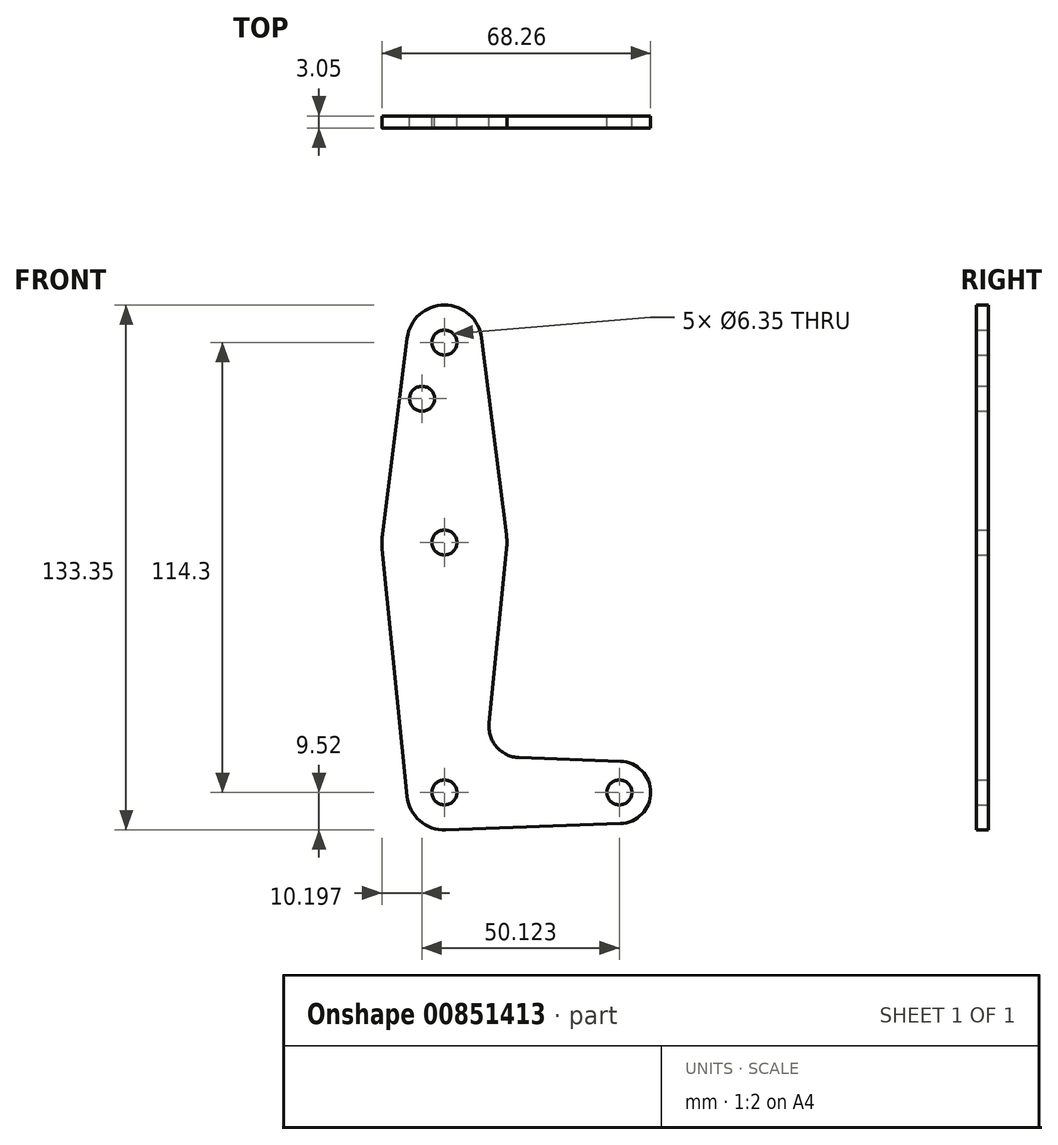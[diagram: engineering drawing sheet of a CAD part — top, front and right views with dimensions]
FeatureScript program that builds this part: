
annotation { "Feature Type Name" : "Feature", "Feature Type Description" : "" }
export const myFeature = defineFeature(function(context is Context, id is Id, definition is map)
    precondition{}
    {
        {
            var Q0;
            Q0=qCreatedBy(makeId("Front.planeOp"),FACE);
            var sketch = newSketch(context, id + "F0", { "sketchPlane" : qUnion([Q0])});
            skLineSegment(sketch, "E0", {"start": v(0, 0) * mm, "end": v(0, 114.3) * mm, "construction": true});
            skLineSegment(sketch, "E1", {"start": v(0, 0) * mm, "end": v(44.45, 0) * mm, "construction": true});
            skCircle(sketch, "E2", {"center": v(0, 0) * mm, "radius": 9.53 * mm});
            skCircle(sketch, "E3", {"center": v(0, 114.3) * mm, "radius": 9.53 * mm});
            skCircle(sketch, "E4", {"center": v(44.45, 0) * mm, "radius": 7.94 * mm});
            skCircle(sketch, "E5", {"center": v(0, 63.5) * mm, "radius": 15.88 * mm});
            skLineSegment(sketch, "E6", {"start": v(11.34, 17.6) * mm, "end": v(15.8, 61.91) * mm});
            skLineSegment(sketch, "E7", {"start": v(-9.48, -0.95) * mm, "end": v(-15.8, 61.91) * mm});
            skLineSegment(sketch, "E8", {"start": v(9.45, 115.5) * mm, "end": v(15.75, 65.48) * mm});
            skLineSegment(sketch, "E9", {"start": v(-9.45, 115.5) * mm, "end": v(-15.75, 65.48) * mm});
            skLineSegment(sketch, "E10", {"start": v(18.97, 8.85) * mm, "end": v(44.73, 7.93) * mm});
            skLineSegment(sketch, "E11", {"start": v(0.34, -9.52) * mm, "end": v(44.73, -7.93) * mm});
            skCircle(sketch, "E12", {"center": v(-5.67, 100.03) * mm, "radius": 3.18 * mm});
            skCircle(sketch, "E13", {"center": v(0, 114.3) * mm, "radius": 3.18 * mm});
            skCircle(sketch, "E14", {"center": v(0, 63.5) * mm, "radius": 3.18 * mm});
            skCircle(sketch, "E15", {"center": v(0, 0) * mm, "radius": 3.18 * mm});
            skCircle(sketch, "E16", {"center": v(44.45, 0) * mm, "radius": 3.18 * mm});
            skArc(sketch, "E17.filletArc", {"start": v(11.34, 17.6) * mm, "mid": v(13.26, 11.57) * mm, "end": v(18.97, 8.85) * mm});
            skSolve(sketch);
        }
        {
            var Q0;
            Q0=makeQuery(id+"F0.imprint","IMPRINT",FACE,{"disambiguationData":[TD([[makeQuery(id+"F0.imprint","IMPRINT",EDGE,{"derivedFrom":sQuery(id+"F0.wireOp",EDGE,"E13")}),-1.0]])]});
            var Q1;
            {var subQ0=sQuery(id+"F0.wireOp",EDGE,"E8");Q1=makeQuery(id+"F0.imprint","IMPRINT",FACE,{"disambiguationData":[TD([[makeQuery(id+"F0.imprint","IMPRINT",EDGE,{"derivedFrom":subQ0}),-1.0]])]});}
            var Q2;
            Q2=makeQuery(id+"F0.imprint","IMPRINT",FACE,{"disambiguationData":[TD([[makeQuery(id+"F0.imprint","IMPRINT",EDGE,{"derivedFrom":sQuery(id+"F0.wireOp",EDGE,"E14")}),-1.0]])]});
            var Q3;
            {var subQ0=sQuery(id+"F0.wireOp",EDGE,"E6");Q3=makeQuery(id+"F0.imprint","IMPRINT",FACE,{"disambiguationData":[TD([[makeQuery(id+"F0.imprint","IMPRINT",EDGE,{"derivedFrom":subQ0}),1.0]])]});}
            var Q4;
            Q4=makeQuery(id+"F0.imprint","IMPRINT",FACE,{"disambiguationData":[TD([[makeQuery(id+"F0.imprint","IMPRINT",EDGE,{"derivedFrom":sQuery(id+"F0.wireOp",EDGE,"E15")}),-1.0]])]});
            var Q5;
            Q5=makeQuery(id+"F0.imprint","IMPRINT",FACE,{"disambiguationData":[TD([[makeQuery(id+"F0.imprint","IMPRINT",EDGE,{"derivedFrom":sQuery(id+"F0.wireOp",EDGE,"E16")}),-1.0]])]});
            extrude(context, id + "F1", {"entities" : qUnion([Q0, Q1, Q2, Q3, Q4, Q5]), "depth" : 3.05 * mm, "offsetDistance" : 25.4 * mm});
        }
    });
